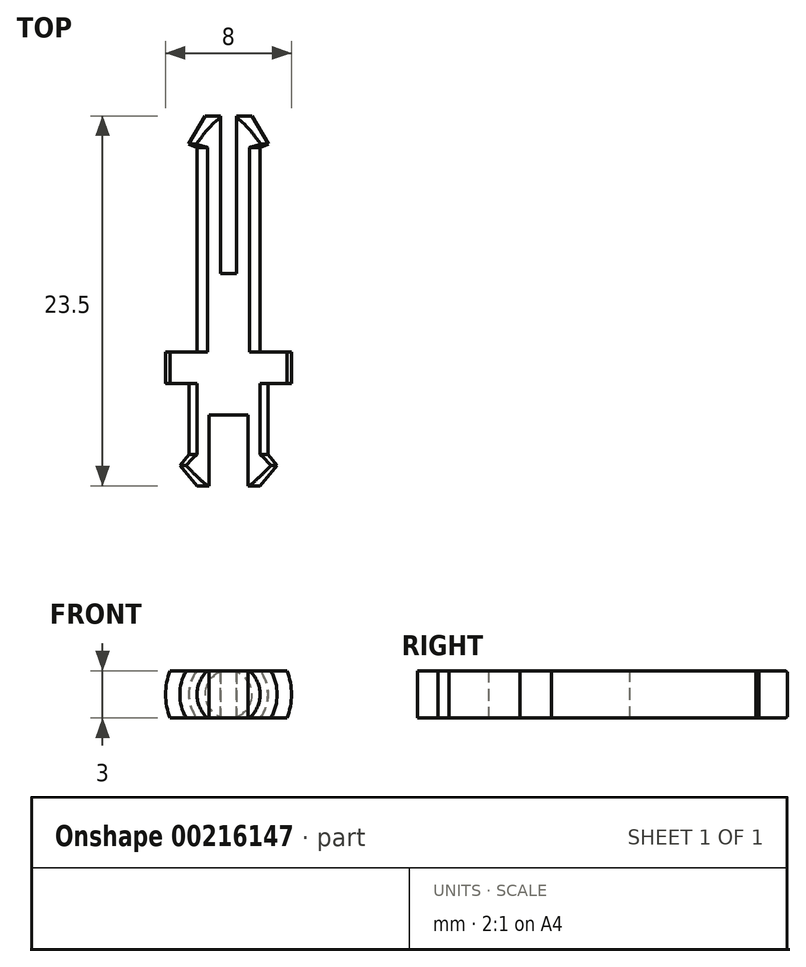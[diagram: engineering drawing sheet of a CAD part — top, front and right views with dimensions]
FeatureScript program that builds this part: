
annotation { "Feature Type Name" : "Feature", "Feature Type Description" : "" }
export const myFeature = defineFeature(function(context is Context, id is Id, definition is map)
    precondition{}
    {
        {
            var Q0;
            Q0=qCreatedBy(makeId("Front.planeOp"),FACE);
            var sketch = newSketch(context, id + "F15", { "sketchPlane" : qUnion([Q0])});
            skCircle(sketch, "E0", {"center": v(0, 0) * mm, "radius": 2.5 * mm});
            skSolve(sketch);
        }
        {
            var Q0;
            Q0 = qSketchRegion(id + "F15", true);
            extrude(context, id + "F0", {"entities" : qUnion([Q0]), "depth" : 4.5 * mm});
        }
        {
            var Q0;
            Q0=qCreatedBy(makeId("Right.planeOp"),FACE);
            var sketch = newSketch(context, id + "F1", { "sketchPlane" : qUnion([Q0])});
            skLineSegment(sketch, "E1", {"start": v(0, 0) * mm, "end": v(-17.97, 0) * mm, "construction": true});
            skLineSegment(sketch, "E2", {"start": v(-4.5, 0) * mm, "end": v(-4.5, 2.5) * mm});
            skLineSegment(sketch, "E3", {"start": v(-4.5, 2.5) * mm, "end": v(-5.2, 3.09) * mm});
            skLineSegment(sketch, "E4", {"start": v(-5.2, 3.09) * mm, "end": v(-6.5, 2) * mm});
            skLineSegment(sketch, "E5", {"start": v(-6.5, 2) * mm, "end": v(-6.5, 0) * mm});
            skLineSegment(sketch, "E6", {"start": v(-6.5, 0) * mm, "end": v(-4.5, 0) * mm});
            skSolve(sketch);
        }
        {
            var Q0;
            Q0 = qSketchRegion(id + "F1", true);
            var Q1;
            Q1=sQuery(id+"F1.wireOp",EDGE,"E1");
            revolve(context, id + "F2", {"operationType" : NewBodyOperationType.ADD, "entities" : qUnion([Q0]), "axis" : qUnion([Q1]), "revolveType" : RevolveType.FULL});
        }
        {
            var Q0;
            Q0=qCreatedBy(makeId("Top.planeOp"),FACE);
            var sketch = newSketch(context, id + "F3", { "sketchPlane" : qUnion([Q0])});
            skLineSegment(sketch, "E7.bottom", {"start": v(-1.25, -2) * mm, "end": v(1.25, -2) * mm});
            skLineSegment(sketch, "E7.top", {"start": v(-1.25, -9) * mm, "end": v(1.25, -9) * mm});
            skLineSegment(sketch, "E7.left", {"start": v(-1.25, -2) * mm, "end": v(-1.25, -9) * mm});
            skLineSegment(sketch, "E7.right", {"start": v(1.25, -2) * mm, "end": v(1.25, -9) * mm});
            skPoint(sketch, "E8", {"position": v(0, -2) * mm});
            skSolve(sketch);
        }
        {
            var Q0;
            Q0 = qSketchRegion(id + "F3", true);
            extrude(context, id + "F4", {"entities" : qUnion([Q0]), "operationType" : NewBodyOperationType.REMOVE, "endBound" : BoundingType.SYMMETRIC, "depth" : 7 * mm});
        }
        {
            var Q0;
            Q0=makeQuery(id+"F15.imprint","IMPRINT",FACE,{"disambiguationData":[TD([[makeQuery(id+"F15.imprint","IMPRINT",EDGE,{"derivedFrom":sQuery(id+"F15.wireOp",EDGE,"E0")}),1.0]])]});
            var sketch = newSketch(context, id + "F5", { "sketchPlane" : qUnion([Q0])});
            skCircle(sketch, "E9", {"center": v(0, 0) * mm, "radius": 4 * mm});
            skSolve(sketch);
        }
        {
            var Q0;
            Q0 = qSketchRegion(id + "F5", true);
            extrude(context, id + "F6", {"entities" : qUnion([Q0]), "operationType" : NewBodyOperationType.ADD, "oppositeDirection" : true, "depth" : 2 * mm});
        }
        {
            var Q0;
            Q0=makeQuery(id+"F6.opExtrude","CAP_FACE",FACE,{"disambiguationData":[OSD([sQuery(id+"F5.wireOp",EDGE,"E9")])],"isStart":false});
            var sketch = newSketch(context, id + "F7", { "sketchPlane" : qUnion([Q0])});
            skCircle(sketch, "E10", {"center": v(0, 0) * mm, "radius": 2 * mm});
            skSolve(sketch);
        }
        {
            var Q0;
            Q0 = qSketchRegion(id + "F7", true);
            extrude(context, id + "F8", {"entities" : qUnion([Q0]), "operationType" : NewBodyOperationType.ADD, "depth" : 13 * mm});
        }
        {
            var Q0;
            Q0=qCreatedBy(makeId("Right.planeOp"),FACE);
            var sketch = newSketch(context, id + "F9", { "sketchPlane" : qUnion([Q0])});
            skLineSegment(sketch, "E11", {"start": v(15, 0) * mm, "end": v(17, 0) * mm});
            skLineSegment(sketch, "E12", {"start": v(17, 0) * mm, "end": v(17, 1.5) * mm});
            skLineSegment(sketch, "E13", {"start": v(17, 1.5) * mm, "end": v(15.2, 2.54) * mm});
            skLineSegment(sketch, "E14", {"start": v(15.2, 2.54) * mm, "end": v(15, 2) * mm});
            skLineSegment(sketch, "E15", {"start": v(15, 2) * mm, "end": v(15, 0) * mm});
            skSolve(sketch);
        }
        {
            var Q0;
            Q0 = qSketchRegion(id + "F9", true);
            var Q1;
            Q1=sQuery(id+"F9.wireOp",EDGE,"E11");
            revolve(context, id + "F10", {"operationType" : NewBodyOperationType.ADD, "entities" : qUnion([Q0]), "axis" : qUnion([Q1]), "revolveType" : RevolveType.FULL});
        }
        {
            var Q0;
            Q0=qCreatedBy(makeId("Top.planeOp"),FACE);
            var sketch = newSketch(context, id + "F11", { "sketchPlane" : qUnion([Q0])});
            skLineSegment(sketch, "E16.bottom", {"start": v(-0.5, 18) * mm, "end": v(0.5, 18) * mm});
            skLineSegment(sketch, "E16.top", {"start": v(-0.5, 7) * mm, "end": v(0.5, 7) * mm});
            skLineSegment(sketch, "E16.left", {"start": v(-0.5, 18) * mm, "end": v(-0.5, 7) * mm});
            skLineSegment(sketch, "E16.right", {"start": v(0.5, 18) * mm, "end": v(0.5, 7) * mm});
            skPoint(sketch, "E17", {"position": v(0, 7) * mm});
            skSolve(sketch);
        }
        {
            var Q0;
            Q0 = qSketchRegion(id + "F11", true);
            extrude(context, id + "F12", {"entities" : qUnion([Q0]), "operationType" : NewBodyOperationType.REMOVE, "endBound" : BoundingType.SYMMETRIC, "oppositeDirection" : true, "depth" : 25 * mm});
        }
        {
            var Q0;
            Q0=qCreatedBy(makeId("Front.planeOp"),FACE);
            var sketch = newSketch(context, id + "F13", { "sketchPlane" : qUnion([Q0])});
            skLineSegment(sketch, "E18.bottom", {"start": v(-5.5, 6.5) * mm, "end": v(5.5, 6.5) * mm});
            skLineSegment(sketch, "E18.top", {"start": v(-5.5, 1.5) * mm, "end": v(5.5, 1.5) * mm});
            skLineSegment(sketch, "E18.left", {"start": v(-5.5, 6.5) * mm, "end": v(-5.5, 1.5) * mm});
            skLineSegment(sketch, "E18.right", {"start": v(5.5, 6.5) * mm, "end": v(5.5, 1.5) * mm});
            skPoint(sketch, "E19", {"position": v(0, 1.5) * mm});
            skLineSegment(sketch, "E20", {"start": v(-5.87, 0) * mm, "end": v(6.42, 0) * mm, "construction": true});
            skPoint(sketch, "E21.MirrorP", {"position": v(0, -1.5) * mm});
            skLineSegment(sketch, "E22.MirrorCS", {"start": v(-5.5, -6.5) * mm, "end": v(5.5, -6.5) * mm});
            skLineSegment(sketch, "E23.MirrorCS", {"start": v(-5.5, -1.5) * mm, "end": v(5.5, -1.5) * mm});
            skLineSegment(sketch, "E24.MirrorCS", {"start": v(-5.5, -6.5) * mm, "end": v(-5.5, -1.5) * mm});
            skLineSegment(sketch, "E25.MirrorCS", {"start": v(5.5, -6.5) * mm, "end": v(5.5, -1.5) * mm});
            skSolve(sketch);
        }
        {
            var Q0;
            Q0 = qSketchRegion(id + "F13", true);
            extrude(context, id + "F14", {"entities" : qUnion([Q0]), "operationType" : NewBodyOperationType.REMOVE, "endBound" : BoundingType.SYMMETRIC, "oppositeDirection" : true, "depth" : 50 * mm});
        }
    });
